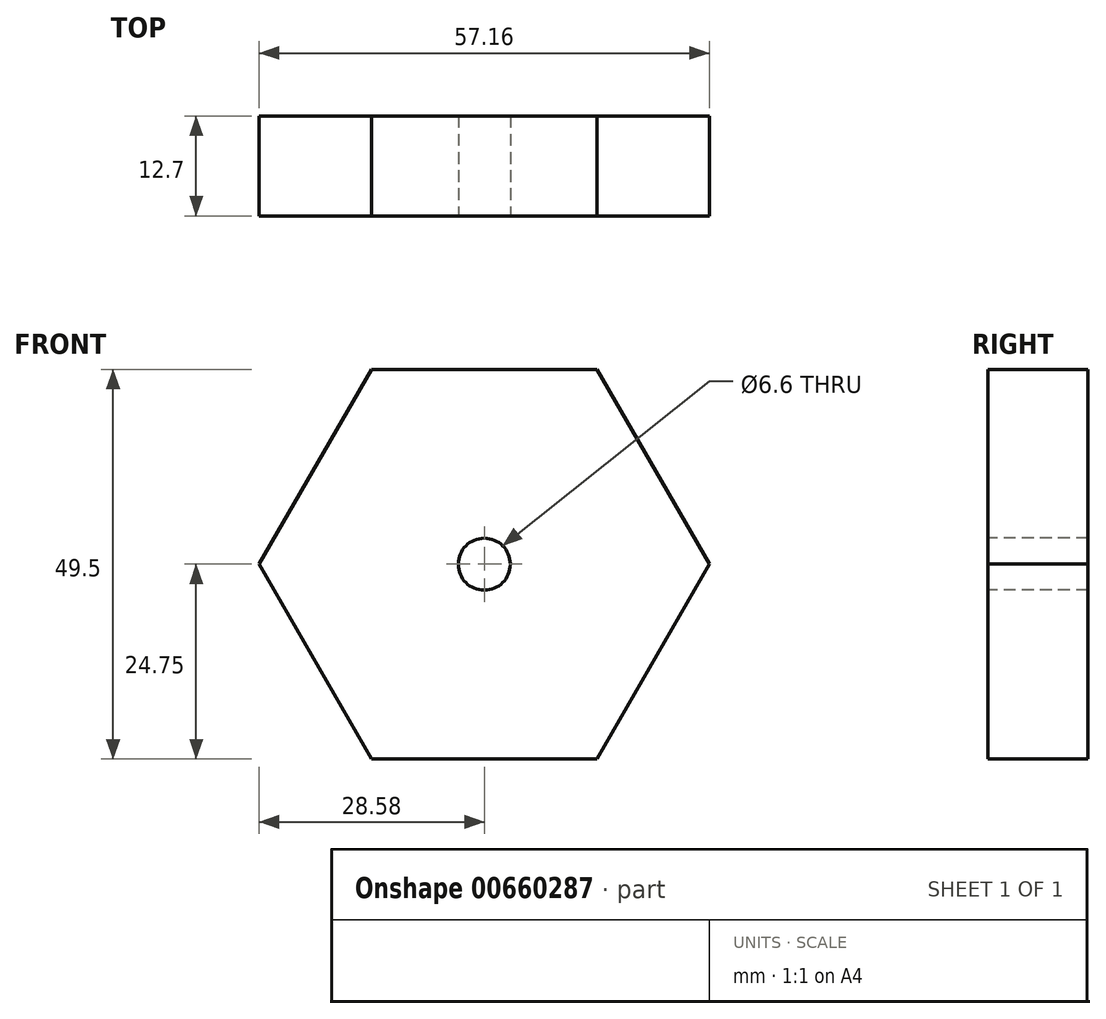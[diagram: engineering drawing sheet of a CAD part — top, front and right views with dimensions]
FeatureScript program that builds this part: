
annotation { "Feature Type Name" : "Feature", "Feature Type Description" : "" }
export const myFeature = defineFeature(function(context is Context, id is Id, definition is map)
    precondition{}
    {
        {
            var Q0;
            Q0=qCreatedBy(makeId("Front.planeOp"),FACE);
            var sketch = newSketch(context, id + "F0", { "sketchPlane" : qUnion([Q0])});
            skCircle(sketch, "E0.cCircle", {"center": v(0, 0) * mm, "radius": 28.58 * mm, "construction": true});
            skLineSegment(sketch, "E0.0", {"start": v(28.57, 0) * mm, "end": v(14.29, -24.75) * mm});
            skLineSegment(sketch, "E0.1", {"start": v(14.29, -24.75) * mm, "end": v(-14.29, -24.75) * mm});
            skLineSegment(sketch, "E0.2", {"start": v(-14.29, -24.75) * mm, "end": v(-28.57, 0) * mm});
            skLineSegment(sketch, "E0.3", {"start": v(-28.58, 0) * mm, "end": v(-14.29, 24.75) * mm});
            skLineSegment(sketch, "E0.4", {"start": v(-14.29, 24.75) * mm, "end": v(14.29, 24.75) * mm});
            skLineSegment(sketch, "E0.5", {"start": v(14.29, 24.75) * mm, "end": v(28.57, 0) * mm});
            skSolve(sketch);
        }
        {
            var Q0;
            Q0=makeQuery(id+"F0.imprint","IMPRINT",FACE,{"disambiguationData":[TD([[makeQuery(id+"F0.imprint","IMPRINT",EDGE,{"derivedFrom":sQuery(id+"F0.wireOp",EDGE,"E0.0")}),-1.0]])]});
            extrude(context, id + "F1", {"entities" : qUnion([Q0]), "depth" : 12.7 * mm, "offsetDistance" : 25.4 * mm});
        }
        {
            var Q0;
            Q0=makeQuery(id+"F1.opExtrude","CAP_FACE",FACE,{"disambiguationData":[OSD([sQuery(id+"F0.wireOp",EDGE,"E0.0"),sQuery(id+"F0.wireOp",EDGE,"E0.1"),sQuery(id+"F0.wireOp",EDGE,"E0.2"),sQuery(id+"F0.wireOp",EDGE,"E0.3"),sQuery(id+"F0.wireOp",EDGE,"E0.4"),sQuery(id+"F0.wireOp",EDGE,"E0.5")])],"isStart":false});
            var sketch = newSketch(context, id + "F2", { "sketchPlane" : qUnion([Q0])});
            skCircle(sketch, "E1", {"center": v(0, 0) * mm, "radius": 3.3 * mm});
            skSolve(sketch);
        }
        {
            var Q0;
            Q0 = qSketchRegion(id + "F2", true);
            extrude(context, id + "F3", {"entities" : qUnion([Q0]), "operationType" : NewBodyOperationType.REMOVE, "oppositeDirection" : true, "depth" : 25.4 * mm, "offsetDistance" : 25.4 * mm});
        }
    });
